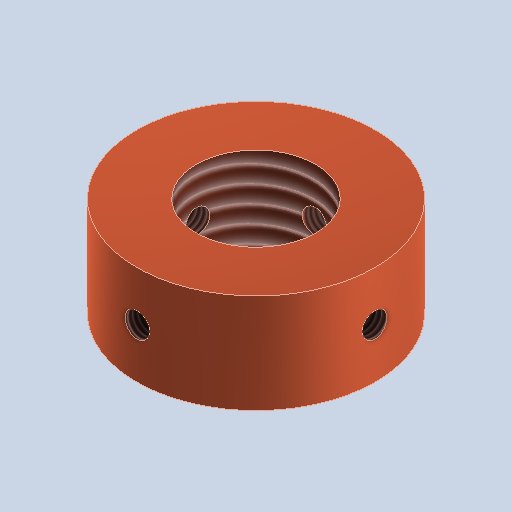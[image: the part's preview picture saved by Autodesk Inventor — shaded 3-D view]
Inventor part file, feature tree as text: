
AUTODESK INVENTOR PART (.ipt)
format: ipt  version: 2025.1 (Build 291241000, 241)  size: 272,896 bytes
history: native  units: mm
features: sketch x2, extrude x1, thread x1, plane x1, hole x1, pattern_circular x1
ambient origin geometry x8: Origin, YZ Plane, XZ Plane, XY Plane, X Axis, Y Axis, Z Axis, Center Point
bodies: Solid1 (feature_tree)
feature tree (7):
  extrude  "Extrusion1"  Depth=10.0mm
  thread  "Thread1"  [1 undecoded]
  plane  "Work Plane1"
  hole  "Hole1"  [1 undecoded]
  pattern_circular  "Circular Pattern1"  Count=4 Angle=360.0deg
  sketch  "Sketch1"  dims[d0=24.0mm d1=12.0mm d2=10.0mm d3=0.0mm]
  sketch  "Sketch2"  dims[d4=10.0mm d5=0.0mm d6=12.0mm d7=2.459mm d8=6.0mm d9=4.0mm d10=2.0mm d11=90.0deg d12=6.5mm d13=0.0mm d14=40.0mm d15=360.0deg]
note: 2 required parameter values undecoded (feature->parameter linkage not recoverable at this tier; creation-order binding heuristic only, values carry confidence <= 0.55)
